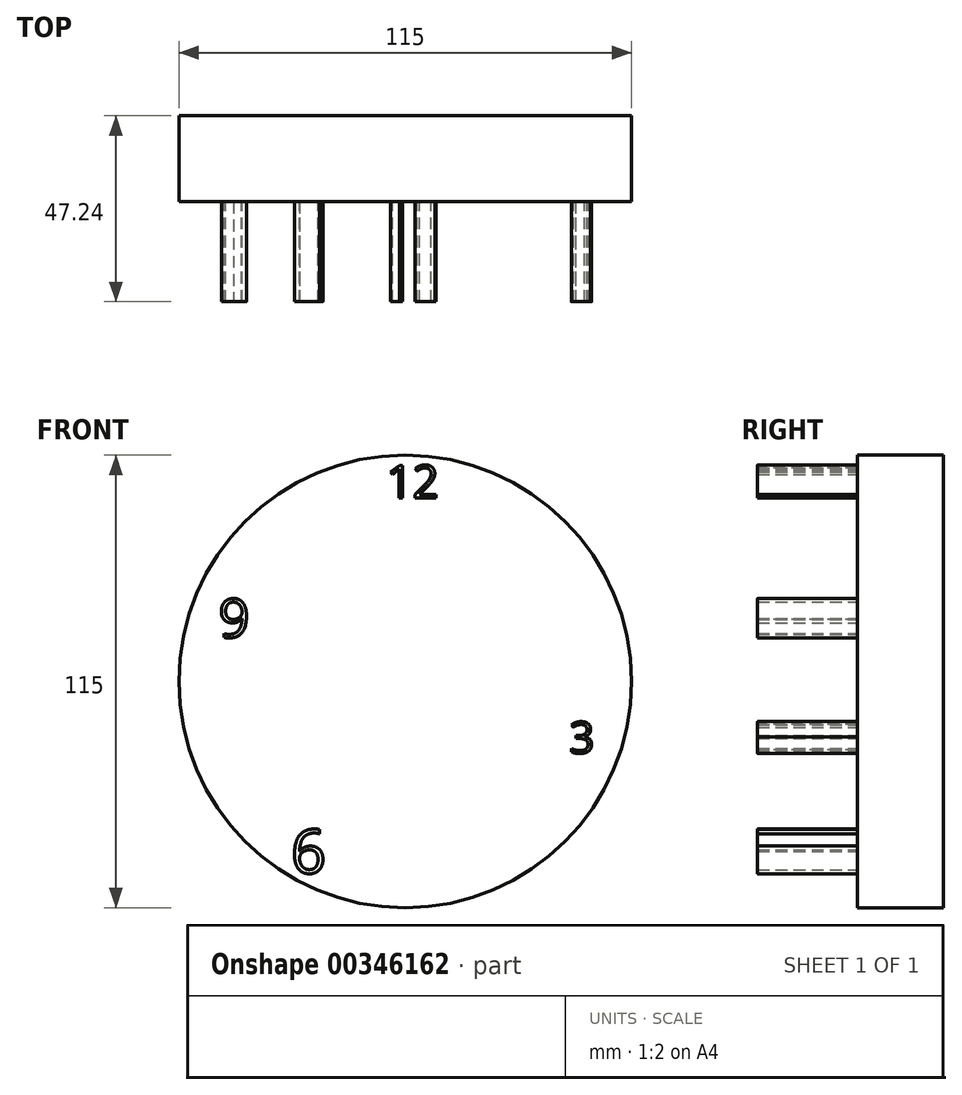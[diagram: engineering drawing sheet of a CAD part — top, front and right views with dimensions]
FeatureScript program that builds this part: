
annotation { "Feature Type Name" : "Feature", "Feature Type Description" : "" }
export const myFeature = defineFeature(function(context is Context, id is Id, definition is map)
    precondition{}
    {
        {
            var Q0;
            Q0=qCreatedBy(makeId("Front.planeOp"),FACE);
            var sketch = newSketch(context, id + "F0", { "sketchPlane" : qUnion([Q0])});
            skCircle(sketch, "E0", {"center": v(1.9, 4.36) * mm, "radius": 57.5 * mm});
            skSolve(sketch);
        }
        {
            var Q0;
            Q0=qCreatedBy(makeId("Front.planeOp"),FACE);
            var sketch = newSketch(context, id + "F1", { "sketchPlane" : qUnion([Q0])});
            skText(sketch, "E1", { "text": "12", "fontName": "OpenSans-Regular.ttf"});
            const initialGuessF1  = {"E1": [-0.00284, 0.051, 1, 0, 0.00834]};
            skSetInitialGuess(sketch, initialGuessF1);
            skSolve(sketch);
        }
        {
            var Q0;
            Q0=qCreatedBy(makeId("Front.planeOp"),FACE);
            var sketch = newSketch(context, id + "F2", { "sketchPlane" : qUnion([Q0])});
            skText(sketch, "E2", { "text": "3", "fontName": "OpenSans-Regular.ttf"});
            const initialGuessF2  = {"E2": [0.0436, -0.01384, 1, 0, 0.00796]};
            skSetInitialGuess(sketch, initialGuessF2);
            skSolve(sketch);
        }
        {
            var Q0;
            Q0=qCreatedBy(makeId("Front.planeOp"),FACE);
            var sketch = newSketch(context, id + "F3", { "sketchPlane" : qUnion([Q0])});
            skText(sketch, "E3", { "text": "6", "fontName": "OpenSans-Regular.ttf"});
            const initialGuessF3  = {"E3": [-0.02711, -0.04437, 1, 0, 0.01119]};
            skSetInitialGuess(sketch, initialGuessF3);
            skSolve(sketch);
        }
        {
            var Q0;
            Q0=qCreatedBy(makeId("Front.planeOp"),FACE);
            var sketch = newSketch(context, id + "F4", { "sketchPlane" : qUnion([Q0])});
            skText(sketch, "E4", { "text": "9", "fontName": "OpenSans-Regular.ttf"});
            const initialGuessF4  = {"E4": [-0.0455, 0.01555, 1, 0, 0.00986]};
            skSetInitialGuess(sketch, initialGuessF4);
            skSolve(sketch);
        }
        {
            var Q0;
            Q0=makeQuery(id+"F0.imprint","IMPRINT",FACE,{"disambiguationData":[TD([[makeQuery(id+"F0.imprint","IMPRINT",EDGE,{"derivedFrom":sQuery(id+"F0.wireOp",EDGE,"E0")}),1.0]])]});
            extrude(context, id + "F5", {"entities" : qUnion([Q0]), "oppositeDirection" : true, "depth" : 21.84 * mm});
        }
        {
            var Q0;
            Q0 = qSketchRegion(id + "F4", true);
            extrude(context, id + "F6", {"entities" : qUnion([Q0]), "operationType" : NewBodyOperationType.ADD, "depth" : 25.4 * mm});
        }
        {
            var Q0;
            Q0 = qSketchRegion(id + "F2", true);
            extrude(context, id + "F7", {"entities" : qUnion([Q0]), "operationType" : NewBodyOperationType.ADD, "depth" : 25.4 * mm});
        }
        {
            var Q0;
            Q0 = qSketchRegion(id + "F3", true);
            extrude(context, id + "F8", {"entities" : qUnion([Q0]), "operationType" : NewBodyOperationType.ADD, "depth" : 25.4 * mm});
        }
        {
            var Q0;
            Q0 = qSketchRegion(id + "F1", true);
            extrude(context, id + "F9", {"entities" : qUnion([Q0]), "operationType" : NewBodyOperationType.ADD, "depth" : 25.4 * mm});
        }
    });
